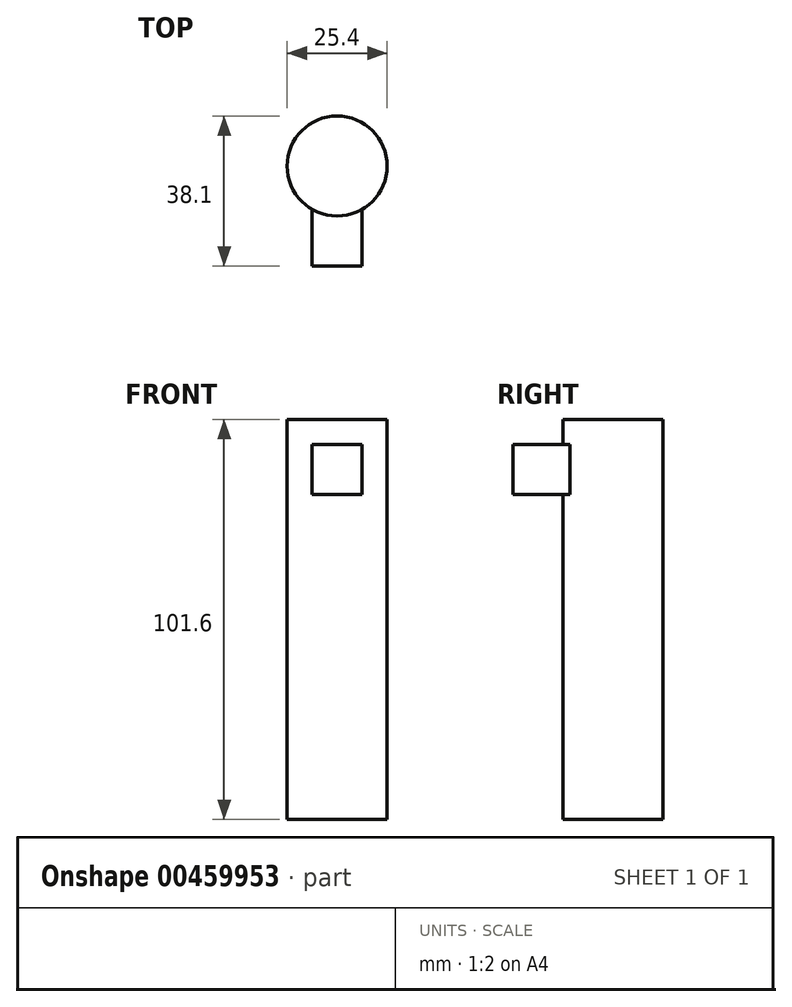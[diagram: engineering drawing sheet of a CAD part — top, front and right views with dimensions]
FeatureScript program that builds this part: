
annotation { "Feature Type Name" : "Feature", "Feature Type Description" : "" }
export const myFeature = defineFeature(function(context is Context, id is Id, definition is map)
    precondition{}
    {
        {
            var Q0;
            Q0=qCreatedBy(makeId("Top.planeOp"),FACE);
            var sketch = newSketch(context, id + "F0", { "sketchPlane" : qUnion([Q0])});
            skCircle(sketch, "E0", {"center": v(0, 0) * mm, "radius": 12.7 * mm});
            skSolve(sketch);
        }
        {
            var Q0;
            Q0=makeQuery(id+"F0.imprint","IMPRINT",FACE,{"disambiguationData":[TD([[makeQuery(id+"F0.imprint","IMPRINT",EDGE,{"derivedFrom":sQuery(id+"F0.wireOp",EDGE,"E0")}),1.0]])]});
            extrude(context, id + "F1", {"entities" : qUnion([Q0]), "depth" : 101.6 * mm});
        }
        {
            var Q0;
            Q0=qCreatedBy(makeId("Front.planeOp"),FACE);
            cPlane(context, id + "F2", {"entities" : qUnion([Q0]), "cplaneType" : CPlaneType.OFFSET, "offset" : 25.4 * mm, "width" : 152.4 * mm, "height" : 152.4 * mm});
        }
        {
            var Q0;
            Q0=qCreatedBy(id+"F2.planeOp",FACE);
            var sketch = newSketch(context, id + "F3", { "sketchPlane" : qUnion([Q0])});
            skLineSegment(sketch, "E1.bottom", {"start": v(-6.35, 95.25) * mm, "end": v(6.35, 95.25) * mm});
            skLineSegment(sketch, "E1.top", {"start": v(-6.35, 82.55) * mm, "end": v(6.35, 82.55) * mm});
            skLineSegment(sketch, "E1.left", {"start": v(-6.35, 95.25) * mm, "end": v(-6.35, 82.55) * mm});
            skLineSegment(sketch, "E1.right", {"start": v(6.35, 95.25) * mm, "end": v(6.35, 82.55) * mm});
            skLineSegment(sketch, "E2.0", {"start": v(-12.7, 101.6) * mm, "end": v(12.7, 101.6) * mm, "construction": true});
            skLineSegment(sketch, "E3", {"start": v(0, 101.6) * mm, "end": v(0, 62.07) * mm, "construction": true});
            skPoint(sketch, "E3.endSnap0", {"position": v(0, 101.6) * mm});
            skSolve(sketch);
        }
        {
            var Q0;
            Q0=makeQuery(id+"F3.imprint","IMPRINT",FACE,{"disambiguationData":[TD([[makeQuery(id+"F3.imprint","IMPRINT",EDGE,{"derivedFrom":sQuery(id+"F3.wireOp",EDGE,"E1.bottom")}),-1.0]])]});
            extrude(context, id + "F4", {"entities" : qUnion([Q0]), "operationType" : NewBodyOperationType.ADD, "endBound" : BoundingType.UP_TO_NEXT, "oppositeDirection" : true, "depth" : 25.4 * mm});
        }
    });
